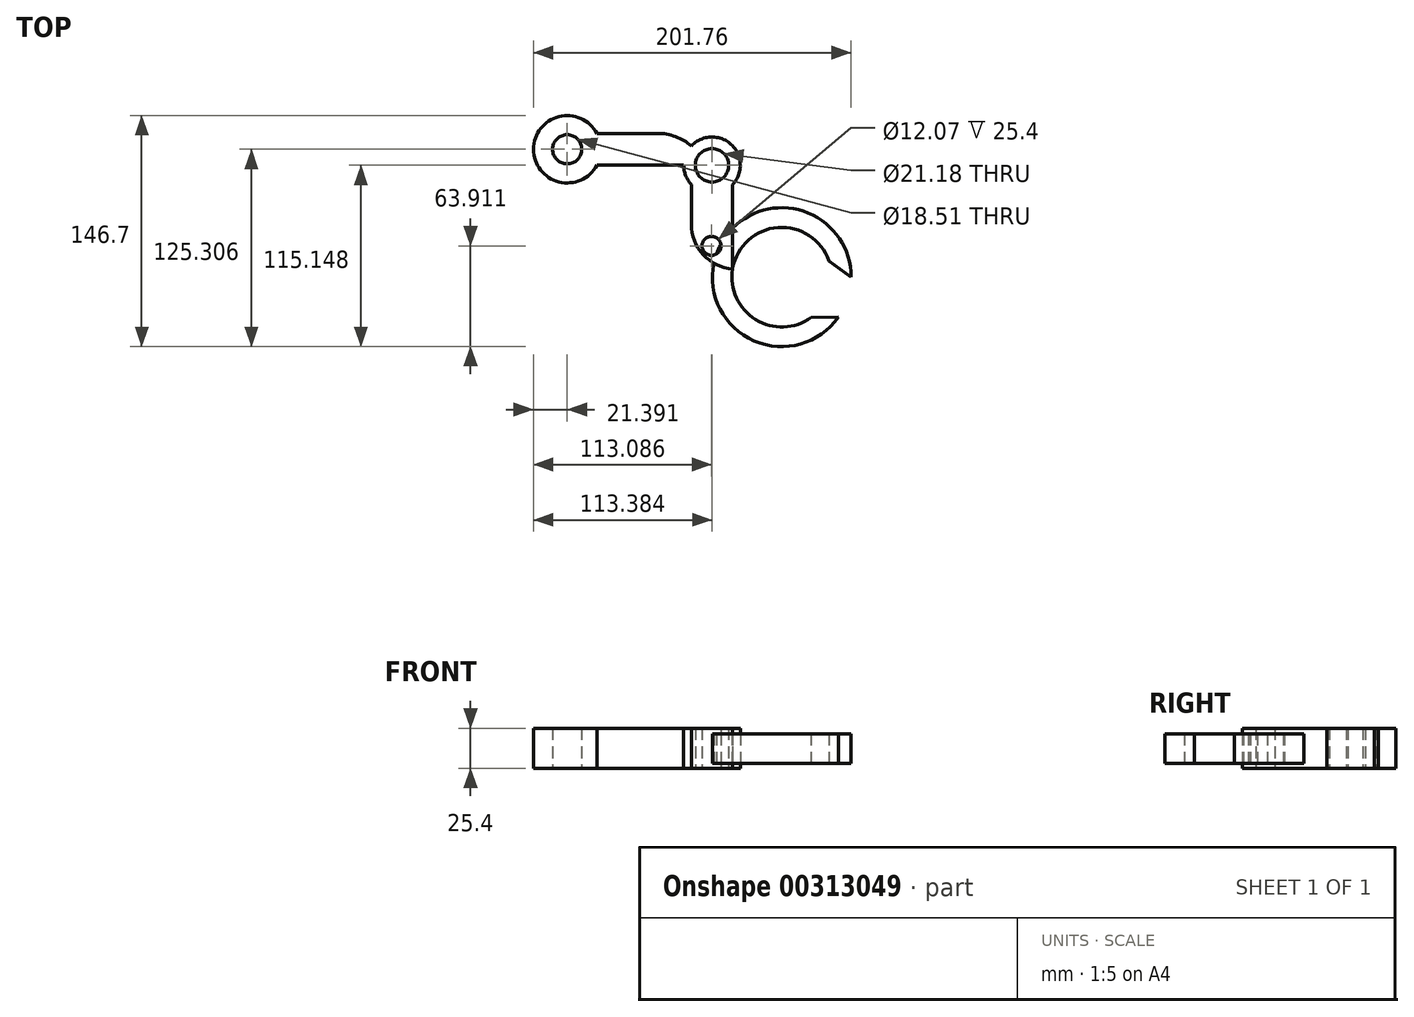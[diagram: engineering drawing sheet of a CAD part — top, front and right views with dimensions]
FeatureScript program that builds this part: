
annotation { "Feature Type Name" : "Feature", "Feature Type Description" : "" }
export const myFeature = defineFeature(function(context is Context, id is Id, definition is map)
    precondition{}
    {
        {
            var Q0;
            Q0=qCreatedBy(makeId("Front.planeOp"),FACE);
            var sketch = newSketch(context, id + "F0", { "sketchPlane" : qUnion([Q0])});
            skLineSegment(sketch, "E0", {"start": v(0, 24.85) * mm, "end": v(0, -24.26) * mm});
            skLineSegment(sketch, "E1.bottom", {"start": v(31.65, 21.89) * mm, "end": v(44.07, 21.89) * mm});
            skLineSegment(sketch, "E1.top", {"start": v(31.65, 3.25) * mm, "end": v(44.07, 3.25) * mm});
            skLineSegment(sketch, "E1.left", {"start": v(31.65, 21.89) * mm, "end": v(31.65, 3.25) * mm});
            skLineSegment(sketch, "E1.right", {"start": v(44.07, 21.89) * mm, "end": v(44.07, 3.25) * mm});
            skSolve(sketch);
        }
        {
            var Q0;
            Q0=makeQuery(id+"F0.imprint","IMPRINT",FACE,{"disambiguationData":[TD([[makeQuery(id+"F0.imprint","IMPRINT",EDGE,{"derivedFrom":sQuery(id+"F0.wireOp",EDGE,"E1.bottom")}),-1.0]])]});
            var Q1;
            Q1=sQuery(id+"F0.wireOp",EDGE,"E0");
            revolve(context, id + "F1", {"entities" : qUnion([Q0]), "axis" : qUnion([Q1]), "revolveType" : RevolveType.ONE_DIRECTION, "oppositeDirection" : true, "angle" : 325 * degree});
        }
        {
            var Q0;
            Q0=qCreatedBy(makeId("Top.planeOp"),FACE);
            var sketch = newSketch(context, id + "F2", { "sketchPlane" : qUnion([Q0])});
            skLineSegment(sketch, "E2", {"start": v(-57.47, 5.06) * mm, "end": v(-57.47, 71.13) * mm});
            skLineSegment(sketch, "E3", {"start": v(-57.47, 5.06) * mm, "end": v(-31.14, 5.06) * mm});
            skLineSegment(sketch, "E4", {"start": v(-31.14, 5.06) * mm, "end": v(-31.14, 71.02) * mm});
            skLineSegment(sketch, "E5", {"start": v(-31.14, 71.02) * mm, "end": v(-57.47, 71.13) * mm});
            skCircle(sketch, "E6", {"center": v(-44.6, 19.84) * mm, "radius": 12.32 * mm});
            skCircle(sketch, "E7", {"center": v(-44.6, 19.84) * mm, "radius": 6.03 * mm});
            skCircle(sketch, "E8", {"center": v(-44.3, 71.08) * mm, "radius": 17.95 * mm});
            skCircle(sketch, "E9", {"center": v(-44.3, 71.08) * mm, "radius": 10.59 * mm});
            skLineSegment(sketch, "E10.bottom", {"start": v(-57.47, 71.13) * mm, "end": v(-136.3, 71.13) * mm});
            skLineSegment(sketch, "E10.top", {"start": v(-57.47, 91.34) * mm, "end": v(-136.3, 91.34) * mm});
            skLineSegment(sketch, "E10.left", {"start": v(-57.47, 71.13) * mm, "end": v(-57.47, 91.34) * mm});
            skLineSegment(sketch, "E10.right", {"start": v(-136.3, 71.13) * mm, "end": v(-136.3, 91.34) * mm});
            skCircle(sketch, "E11", {"center": v(-136.3, 81.24) * mm, "radius": 21.4 * mm});
            skCircle(sketch, "E12", {"center": v(-136.3, 81.24) * mm, "radius": 9.25 * mm});
            skSolve(sketch);
        }
        {
            var Q0;
            Q0=makeQuery(id+"F2.imprint","IMPRINT",FACE,{"disambiguationData":[TD([[makeQuery(id+"F2.imprint","IMPRINT",EDGE,{"derivedFrom":sQuery(id+"F2.wireOp",EDGE,"E6")}),1.0]])]});
            var Q1;
            Q1=makeQuery(id+"F2.imprint","IMPRINT",FACE,{"disambiguationData":[TD([[makeQuery(id+"F2.imprint","IMPRINT",EDGE,{"derivedFrom":sQuery(id+"F2.wireOp",EDGE,"E2")}),-1.0]])]});
            extrude(context, id + "F3", {"entities" : qUnion([Q0, Q1]), "operationType" : NewBodyOperationType.ADD, "depth" : 25.4 * mm});
        }
        {
            var Q0;
            Q0=makeQuery(id+"F1.opRevolve","CAP_EDGE",EDGE,{"disambiguationData":[OSD([sQuery(id+"F0.wireOp",EDGE,"E1.left")])],"isStart":false});
            chamfer(context, id + "F4", {"entities" : qUnion([Q0]), "width" : 15.24 * mm, "tangentPropagation" : true});
        }
        {
            var Q0;
            Q0=makeQuery(id+"F1.opRevolve","CAP_EDGE",EDGE,{"disambiguationData":[OSD([sQuery(id+"F0.wireOp",EDGE,"E1.left")])],"isStart":true});
            chamfer(context, id + "F5", {"entities" : qUnion([Q0]), "width" : 15.24 * mm, "tangentPropagation" : true});
        }
        {
            var Q0;
            Q0=makeQuery(id+"F3.opExtrude","SWEPT_EDGE",EDGE,{"disambiguationData":[OSD([sQuery(id+"F2.wireOp",EDGE,"E2"),sQuery(id+"F2.wireOp",EDGE,"E3")])]});
            fillet(context, id + "F6", {"entities" : qUnion([Q0]), "radius" : 27.6 * mm, "tangentPropagation" : true, "allowEdgeOverflow" : false});
        }
        {
            var Q0;
            Q0 = qSketchRegion(id + "F2", true);
            extrude(context, id + "F7", {"entities" : qUnion([Q0]), "operationType" : NewBodyOperationType.ADD, "depth" : 25.4 * mm});
        }
        {
            var Q0;
            Q0=makeQuery(id+"F7.opExtrude","SWEPT_EDGE",EDGE,{"disambiguationData":[OSD([sQuery(id+"F2.wireOp",EDGE,"E2"),sQuery(id+"F2.wireOp",EDGE,"E3")])]});
            fillet(context, id + "F8", {"entities" : qUnion([Q0]), "radius" : 28.82 * mm, "tangentPropagation" : true, "allowEdgeOverflow" : false});
        }
        {
            var Q0;
            Q0=makeQuery(id+"F7.opExtrude","SWEPT_EDGE",EDGE,{"disambiguationData":[OSD([sQuery(id+"F2.wireOp",EDGE,"E10.top"),sQuery(id+"F2.wireOp",EDGE,"E10.left")])]});
            fillet(context, id + "F9", {"entities" : qUnion([Q0]), "radius" : 32.5 * mm, "tangentPropagation" : true, "allowEdgeOverflow" : false});
        }
    });
